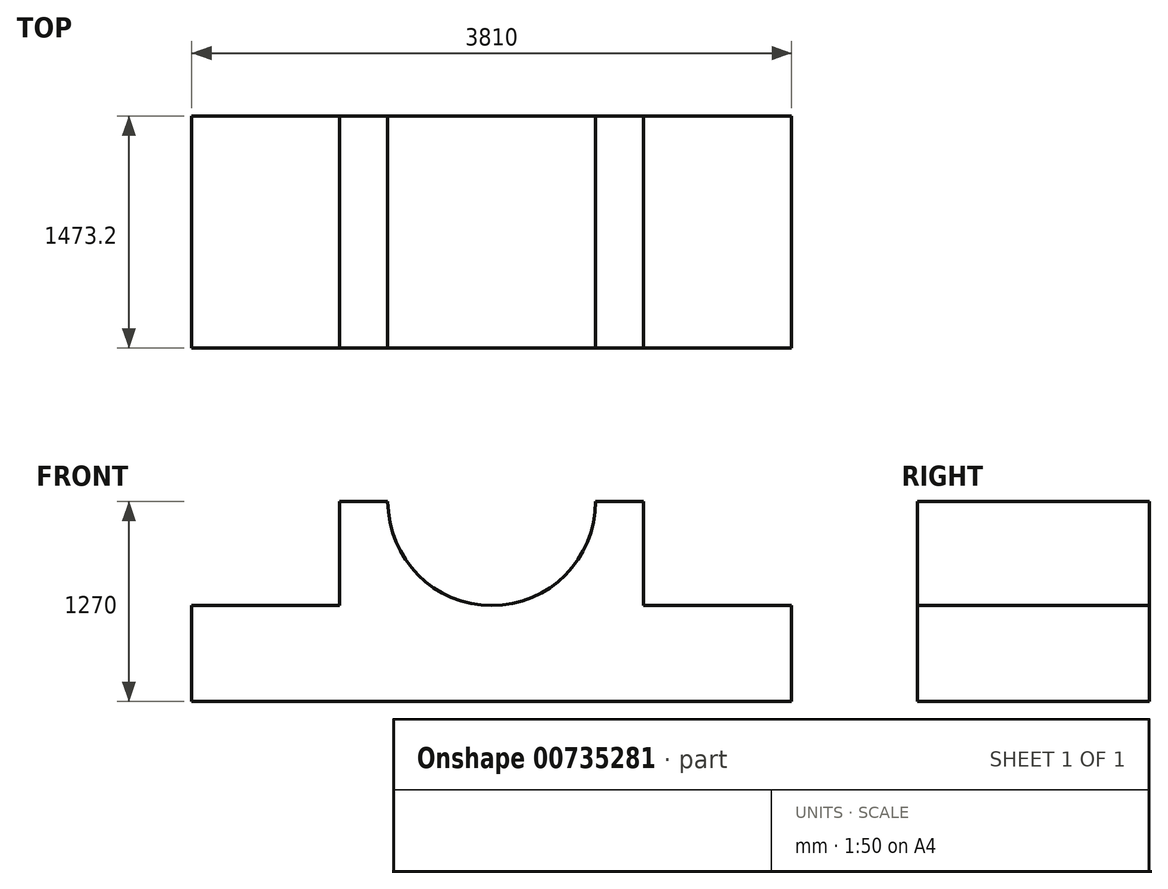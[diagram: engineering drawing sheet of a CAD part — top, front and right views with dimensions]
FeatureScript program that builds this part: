
annotation { "Feature Type Name" : "Feature", "Feature Type Description" : "" }
export const myFeature = defineFeature(function(context is Context, id is Id, definition is map)
    precondition{}
    {
        {
            var Q0;
            Q0=qCreatedBy(makeId("Front.planeOp"),FACE);
            var sketch = newSketch(context, id + "F0", { "sketchPlane" : qUnion([Q0])});
            skLineSegment(sketch, "E0", {"start": v(-97.2, -22.7) * mm, "end": v(3712.8, -22.7) * mm});
            skLineSegment(sketch, "E1", {"start": v(-97.2, -22.7) * mm, "end": v(-97.2, 586.9) * mm});
            skLineSegment(sketch, "E2", {"start": v(3712.8, -22.7) * mm, "end": v(3712.8, 586.9) * mm});
            skLineSegment(sketch, "E3", {"start": v(3712.8, 586.9) * mm, "end": v(2773, 586.9) * mm});
            skLineSegment(sketch, "E4", {"start": v(-97.2, 586.9) * mm, "end": v(842.6, 586.9) * mm});
            skLineSegment(sketch, "E5", {"start": v(842.6, 586.9) * mm, "end": v(842.6, 1247.3) * mm});
            skLineSegment(sketch, "E6", {"start": v(842.6, 1247.3) * mm, "end": v(1147.4, 1247.3) * mm});
            skLineSegment(sketch, "E7", {"start": v(2773, 586.9) * mm, "end": v(2773, 1247.3) * mm});
            skLineSegment(sketch, "E8", {"start": v(2773, 1247.3) * mm, "end": v(2468.2, 1247.3) * mm});
            skCircle(sketch, "E9", {"center": v(1807.8, 1247.3) * mm, "radius": 660.4 * mm});
            skSolve(sketch);
        }
        {
            var Q0;
            Q0=makeQuery(id+"F0.imprint","IMPRINT",FACE,{"disambiguationData":[TD([[makeQuery(id+"F0.imprint","IMPRINT",EDGE,{"derivedFrom":sQuery(id+"F0.wireOp",EDGE,"E0")}),1.0]])]});
            extrude(context, id + "F1", {"entities" : qUnion([Q0]), "depth" : 1473.2 * mm, "offsetDistance" : 25.4 * mm});
        }
    });
